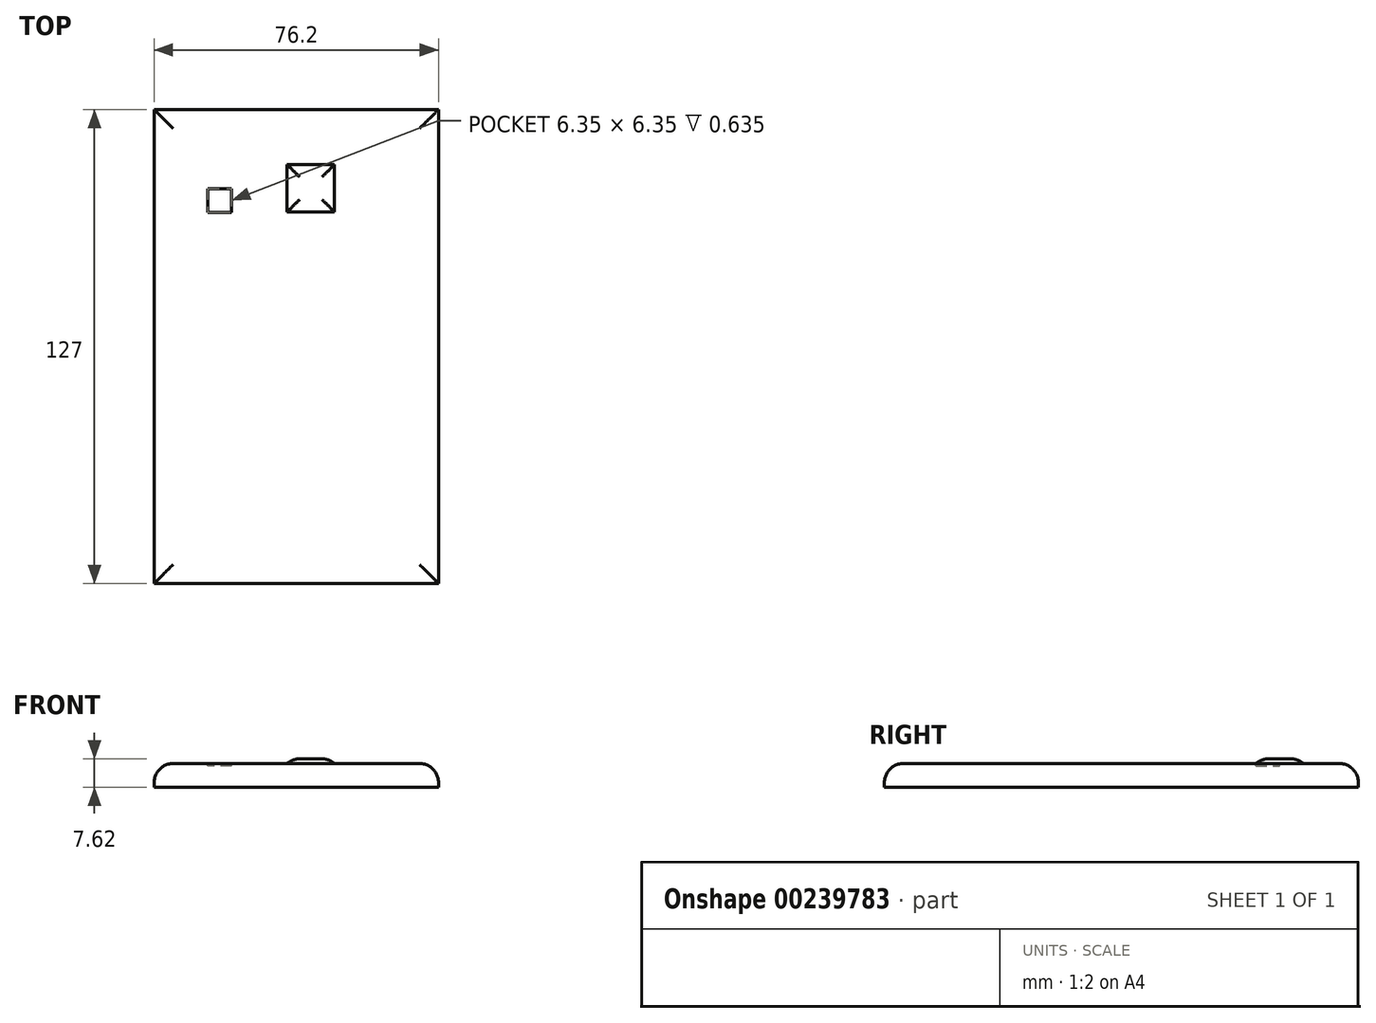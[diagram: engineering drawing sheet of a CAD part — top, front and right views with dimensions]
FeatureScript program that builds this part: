
annotation { "Feature Type Name" : "Feature", "Feature Type Description" : "" }
export const myFeature = defineFeature(function(context is Context, id is Id, definition is map)
    precondition{}
    {
        {
            var Q0;
            Q0=qCreatedBy(makeId("Top.planeOp"),FACE);
            var sketch = newSketch(context, id + "F0", { "sketchPlane" : qUnion([Q0])});
            skLineSegment(sketch, "E0.bottom", {"start": v(38.1, 63.5) * mm, "end": v(-38.1, 63.5) * mm});
            skLineSegment(sketch, "E0.top", {"start": v(38.1, -63.5) * mm, "end": v(-38.1, -63.5) * mm});
            skLineSegment(sketch, "E0.left", {"start": v(38.1, 63.5) * mm, "end": v(38.1, -63.5) * mm});
            skLineSegment(sketch, "E0.right", {"start": v(-38.1, 63.5) * mm, "end": v(-38.1, -63.5) * mm});
            skPoint(sketch, "E0.middle", {"position": v(0, 0) * mm});
            skSolve(sketch);
        }
        {
            var Q0;
            Q0 = qSketchRegion(id + "F0", true);
            extrude(context, id + "F1", {"entities" : qUnion([Q0]), "depth" : 6.35 * mm});
        }
        {
            var Q0;
            Q0=makeQuery(id+"F1.opExtrude","CAP_FACE",FACE,{"disambiguationData":[OSD([sQuery(id+"F0.wireOp",EDGE,"E0.bottom"),sQuery(id+"F0.wireOp",EDGE,"E0.top"),sQuery(id+"F0.wireOp",EDGE,"E0.left"),sQuery(id+"F0.wireOp",EDGE,"E0.right")])],"isStart":false});
            var sketch = newSketch(context, id + "F2", { "sketchPlane" : qUnion([Q0])});
            skLineSegment(sketch, "E1.bottom", {"start": v(-2.46, 48.76) * mm, "end": v(10.24, 48.76) * mm});
            skLineSegment(sketch, "E1.top", {"start": v(-2.46, 36.06) * mm, "end": v(10.24, 36.06) * mm});
            skLineSegment(sketch, "E1.left", {"start": v(-2.46, 48.76) * mm, "end": v(-2.46, 36.06) * mm});
            skLineSegment(sketch, "E1.right", {"start": v(10.24, 48.76) * mm, "end": v(10.24, 36.06) * mm});
            skSolve(sketch);
        }
        {
            var Q0;
            Q0 = qSketchRegion(id + "F2", true);
            extrude(context, id + "F3", {"entities" : qUnion([Q0]), "operationType" : NewBodyOperationType.ADD, "depth" : 1.27 * mm});
        }
        {
            var Q0;
            Q0=makeQuery(id+"F1.opExtrude","CAP_FACE",FACE,{"disambiguationData":[OSD([sQuery(id+"F0.wireOp",EDGE,"E0.bottom"),sQuery(id+"F0.wireOp",EDGE,"E0.top"),sQuery(id+"F0.wireOp",EDGE,"E0.left"),sQuery(id+"F0.wireOp",EDGE,"E0.right")])],"isStart":false});
            var sketch = newSketch(context, id + "F4", { "sketchPlane" : qUnion([Q0])});
            skLineSegment(sketch, "E2.bottom", {"start": v(-17.35, 35.98) * mm, "end": v(-23.7, 35.98) * mm});
            skLineSegment(sketch, "E2.top", {"start": v(-17.35, 42.33) * mm, "end": v(-23.7, 42.33) * mm});
            skLineSegment(sketch, "E2.left", {"start": v(-17.35, 35.98) * mm, "end": v(-17.35, 42.33) * mm});
            skLineSegment(sketch, "E2.right", {"start": v(-23.7, 35.98) * mm, "end": v(-23.7, 42.33) * mm});
            skPoint(sketch, "E2.middle", {"position": v(-20.52, 39.15) * mm});
            skSolve(sketch);
        }
        {
            var Q0;
            Q0 = qSketchRegion(id + "F4", true);
            extrude(context, id + "F5", {"entities" : qUnion([Q0]), "operationType" : NewBodyOperationType.REMOVE, "oppositeDirection" : true, "depth" : 0.64 * mm});
        }
        {
            var Q0;
            Q0=makeQuery(id+"F3.opExtrude","CAP_FACE",FACE,{"disambiguationData":[OSD([sQuery(id+"F2.wireOp",EDGE,"E1.bottom"),sQuery(id+"F2.wireOp",EDGE,"E1.top"),sQuery(id+"F2.wireOp",EDGE,"E1.left"),sQuery(id+"F2.wireOp",EDGE,"E1.right")])],"isStart":false});
            var Q1;
            Q1=makeQuery(id+"F1.opExtrude","CAP_EDGE",EDGE,{"disambiguationData":[OSD([sQuery(id+"F0.wireOp",EDGE,"E0.left")])],"isStart":false});
            var Q2;
            Q2=makeQuery(id+"F1.opExtrude","CAP_EDGE",EDGE,{"disambiguationData":[OSD([sQuery(id+"F0.wireOp",EDGE,"E0.top")])],"isStart":false});
            var Q3;
            Q3=makeQuery(id+"F1.opExtrude","CAP_EDGE",EDGE,{"disambiguationData":[OSD([sQuery(id+"F0.wireOp",EDGE,"E0.right")])],"isStart":false});
            var Q4;
            Q4=makeQuery(id+"F1.opExtrude","CAP_EDGE",EDGE,{"disambiguationData":[OSD([sQuery(id+"F0.wireOp",EDGE,"E0.bottom")])],"isStart":false});
            fillet(context, id + "F6", {"entities" : qUnion([Q0, Q1, Q2, Q3, Q4]), "radius" : 5.08 * mm, "tangentPropagation" : true, "allowEdgeOverflow" : false});
        }
    });
